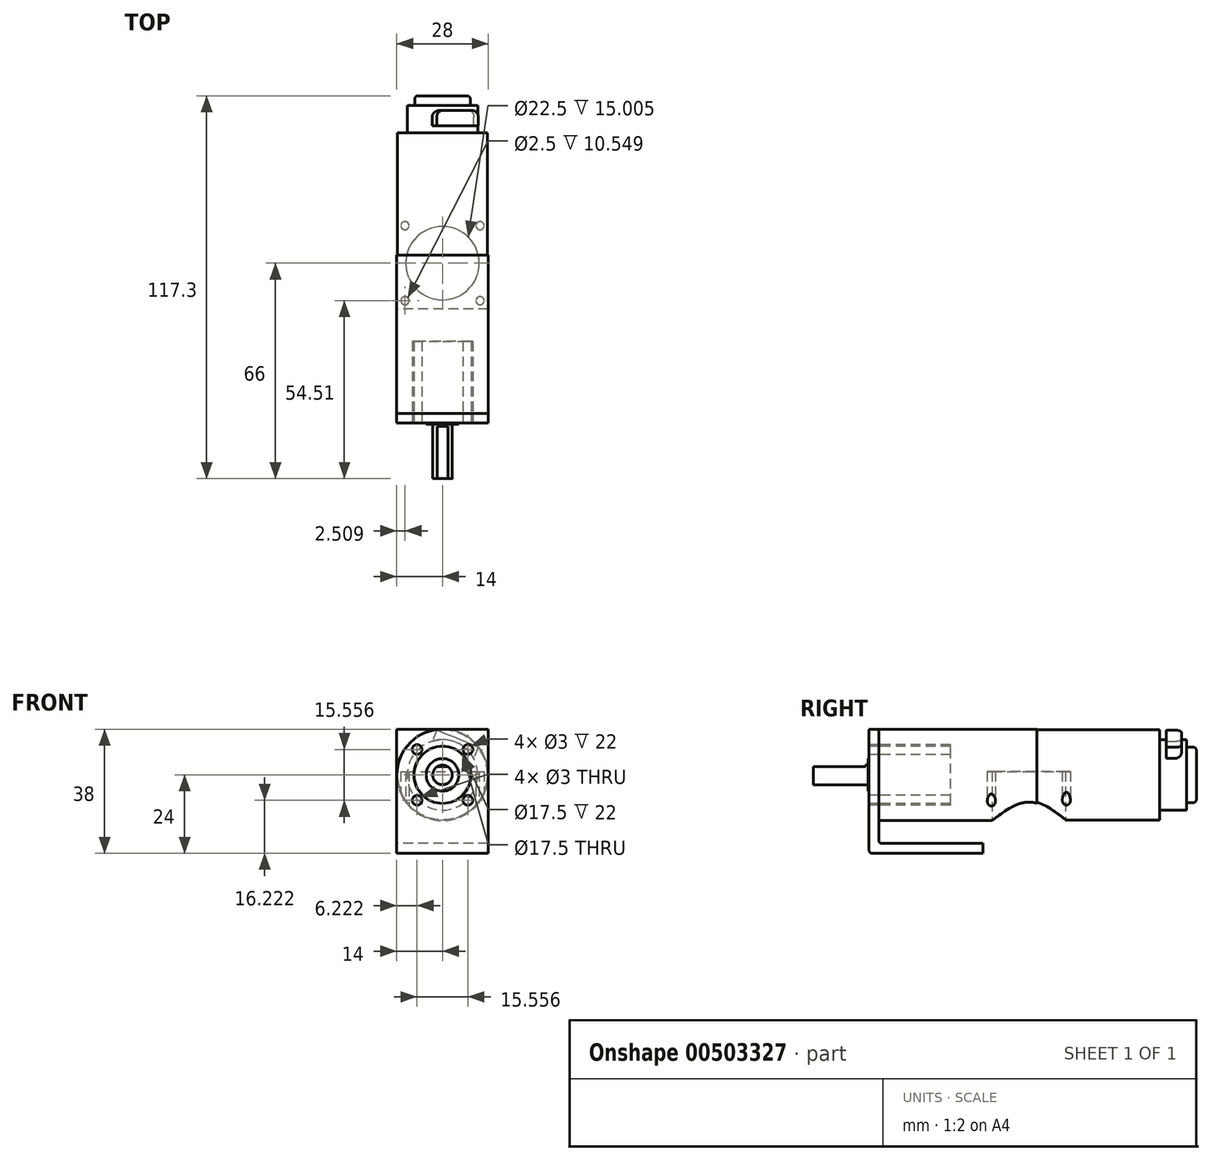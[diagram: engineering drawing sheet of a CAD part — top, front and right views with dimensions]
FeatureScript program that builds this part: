
annotation { "Feature Type Name" : "Feature", "Feature Type Description" : "" }
export const myFeature = defineFeature(function(context is Context, id is Id, definition is map)
    precondition{}
    {
        {
            var Q0;
            Q0=qCreatedBy(makeId("Right.planeOp"),FACE);
            var sketch = newSketch(context, id + "F0", { "sketchPlane" : qUnion([Q0])});
            skLineSegment(sketch, "E0", {"start": v(0, 0) * mm, "end": v(-20, 0) * mm});
            skLineSegment(sketch, "E1", {"start": v(-20, 0) * mm, "end": v(-20, 3) * mm});
            skLineSegment(sketch, "E2", {"start": v(-20, 3) * mm, "end": v(-3.3, 3) * mm});
            skLineSegment(sketch, "E3", {"start": v(-3.3, 3) * mm, "end": v(-3.3, 5) * mm});
            skLineSegment(sketch, "E4", {"start": v(-3.3, 5) * mm, "end": v(-2, 5) * mm});
            skLineSegment(sketch, "E5", {"start": v(-2, 5) * mm, "end": v(-2, 8.5) * mm});
            skLineSegment(sketch, "E6", {"start": v(-2, 8.5) * mm, "end": v(0, 8.5) * mm});
            skLineSegment(sketch, "E7", {"start": v(0, 8.5) * mm, "end": v(0, 14) * mm});
            skLineSegment(sketch, "E8", {"start": v(0, 14) * mm, "end": v(48.5, 14) * mm});
            skLineSegment(sketch, "E9", {"start": v(48.5, 14) * mm, "end": v(48.5, 13.8) * mm});
            skLineSegment(sketch, "E10", {"start": v(48.5, 13.8) * mm, "end": v(86, 13.8) * mm});
            skLineSegment(sketch, "E11", {"start": v(86, 13.8) * mm, "end": v(86, 10.8) * mm});
            skLineSegment(sketch, "E12", {"start": v(86, 10.8) * mm, "end": v(94.3, 10.8) * mm});
            skLineSegment(sketch, "E13", {"start": v(94.3, 10.8) * mm, "end": v(94.3, 8.5) * mm});
            skLineSegment(sketch, "E14", {"start": v(94.3, 8.5) * mm, "end": v(97.3, 8.5) * mm});
            skLineSegment(sketch, "E15", {"start": v(97.3, 8.5) * mm, "end": v(97.3, 0) * mm});
            skLineSegment(sketch, "E16", {"start": v(97.3, 0) * mm, "end": v(0, 0) * mm});
            skSolve(sketch);
        }
        {
            var Q0;
            Q0=makeQuery(id+"F0.imprint","IMPRINT",FACE,{"disambiguationData":[TD([[makeQuery(id+"F0.imprint","IMPRINT",EDGE,{"derivedFrom":sQuery(id+"F0.wireOp",EDGE,"E0")}),-1.0]])]});
            var Q1;
            Q1=sQuery(id+"F0.wireOp",EDGE,"E16");
            revolve(context, id + "F1", {"entities" : qUnion([Q0]), "axis" : qUnion([Q1]), "revolveType" : RevolveType.FULL});
        }
        {
            var Q0;
            Q0=makeQuery(id+"F1.opRevolve","SWEPT_FACE",FACE,{"disambiguationData":[OSD([sQuery(id+"F0.wireOp",EDGE,"E1")])]});
            var sketch = newSketch(context, id + "F2", { "sketchPlane" : qUnion([Q0])});
            skArc(sketch, "E17.0", {"start": v(1.66, 2.5) * mm, "mid": v(0, 3) * mm, "end": v(-1.66, 2.5) * mm});
            skLineSegment(sketch, "E18", {"start": v(-1.66, 2.5) * mm, "end": v(1.66, 2.5) * mm});
            skSolve(sketch);
        }
        {
            var Q0;
            Q0=makeQuery(id+"F2.imprint","IMPRINT",FACE,{"disambiguationData":[TD([[makeQuery(id+"F2.imprint","IMPRINT",EDGE,{"derivedFrom":sQuery(id+"F2.wireOp",EDGE,"E17.0")}),-1.0]])]});
            extrude(context, id + "F3", {"entities" : qUnion([Q0]), "operationType" : NewBodyOperationType.REMOVE, "oppositeDirection" : true, "depth" : 16 * mm});
        }
        {
            var Q0;
            Q0=makeQuery(id+"F1.opRevolve","SWEPT_FACE",FACE,{"disambiguationData":[OSD([sQuery(id+"F0.wireOp",EDGE,"E7")])]});
            var sketch = newSketch(context, id + "F4", { "sketchPlane" : qUnion([Q0])});
            skCircle(sketch, "E19", {"center": v(7.78, 7.78) * mm, "radius": 1.5 * mm});
            skCircle(sketch, "E20.1.0", {"center": v(-7.78, 7.78) * mm, "radius": 1.5 * mm});
            skCircle(sketch, "E20.2.0", {"center": v(-7.78, -7.78) * mm, "radius": 1.5 * mm});
            skCircle(sketch, "E20.3.0", {"center": v(7.78, -7.78) * mm, "radius": 1.5 * mm});
            skPoint(sketch, "E20.center", {"position": v(0, 0) * mm});
            skSolve(sketch);
        }
        {
            var Q0;
            Q0=makeQuery(id+"F4.imprint","IMPRINT",FACE,{"disambiguationData":[TD([[makeQuery(id+"F4.imprint","IMPRINT",EDGE,{"derivedFrom":sQuery(id+"F4.wireOp",EDGE,"E19")}),1.0]])]});
            extrude(context, id + "F5", {"entities" : qUnion([Q0]), "operationType" : NewBodyOperationType.REMOVE, "oppositeDirection" : true, "depth" : 3.5 * mm});
        }
        {
            var Q0;
            Q0=makeQuery(id+"F1.opRevolve","SWEPT_EDGE",EDGE,{"disambiguationData":[OSD([sQuery(id+"F0.wireOp",EDGE,"E14"),sQuery(id+"F0.wireOp",EDGE,"E15")])]});
            fillet(context, id + "F6", {"entities" : qUnion([Q0]), "radius" : 1 * mm, "tangentPropagation" : true, "allowEdgeOverflow" : false});
        }
        {
            var Q0;
            Q0=sQuery(id+"F0.wireOp",EDGE,"E16");
            cPlane(context, id + "F7", {"entities" : qUnion([Q0]), "cplaneType" : CPlaneType.LINE_ANGLE, "offset" : 25 * mm, "angle" : 157.5 * degree, "width" : 150 * mm, "height" : 150 * mm});
        }
        {
            var Q0;
            Q0=qCreatedBy(id+"F7.planeOp",FACE);
            var sketch = newSketch(context, id + "F8", { "sketchPlane" : qUnion([Q0])});
            skLineSegment(sketch, "E21.bottom", {"start": v(6.9, 92.79) * mm, "end": v(-6.9, 92.79) * mm});
            skLineSegment(sketch, "E21.top", {"start": v(6.9, 88.09) * mm, "end": v(-6.9, 88.09) * mm});
            skLineSegment(sketch, "E21.left", {"start": v(6.9, 92.79) * mm, "end": v(6.9, 88.09) * mm});
            skLineSegment(sketch, "E21.right", {"start": v(-6.9, 92.79) * mm, "end": v(-6.9, 88.09) * mm});
            skPoint(sketch, "E21.middle", {"position": v(0, 90.44) * mm});
            skSolve(sketch);
        }
        {
            var Q0;
            Q0=qSketchRegion(id+"F8",true);
            extrude(context, id + "F9", {"entities" : qUnion([Q0]), "operationType" : NewBodyOperationType.ADD, "depth" : 12 * mm});
        }
        {
            var Q0;
            Q0=makeQuery(id+"F9.opExtrude","SWEPT_EDGE",EDGE,{"disambiguationData":[OSD([sQuery(id+"F8.wireOp",EDGE,"E21.bottom"),sQuery(id+"F8.wireOp",EDGE,"E21.left")])]});
            var Q1;
            Q1=makeQuery(id+"F9.opExtrude","SWEPT_EDGE",EDGE,{"disambiguationData":[OSD([sQuery(id+"F8.wireOp",EDGE,"E21.bottom"),sQuery(id+"F8.wireOp",EDGE,"E21.right")])]});
            fillet(context, id + "F10", {"entities" : qUnion([Q0, Q1]), "radius" : 2 * mm, "tangentPropagation" : true, "allowEdgeOverflow" : false});
        }
        {
            var Q0;
            Q0=qCreatedBy(makeId("Right.planeOp"),FACE);
            var sketch = newSketch(context, id + "F11", { "sketchPlane" : qUnion([Q0])});
            skLineSegment(sketch, "E22.0", {"start": v(0, -21) * mm, "end": v(0, 14) * mm});
            skLineSegment(sketch, "E23.0", {"start": v(0, 0) * mm, "end": v(-20, 0) * mm, "construction": true});
            skLineSegment(sketch, "E24", {"start": v(0, 14) * mm, "end": v(-19.97, 14) * mm, "construction": true});
            skPoint(sketch, "E25.orphan", {"position": v(0, 14) * mm});
            skPoint(sketch, "E26.orphan", {"position": v(0, 8.5) * mm});
            skLineSegment(sketch, "E27", {"start": v(0, 14) * mm, "end": v(-3, 14) * mm});
            skLineSegment(sketch, "E28", {"start": v(-3, 14) * mm, "end": v(-3, -24) * mm});
            skLineSegment(sketch, "E29", {"start": v(-3, -24) * mm, "end": v(32, -24) * mm});
            skLineSegment(sketch, "E30", {"start": v(32, -24) * mm, "end": v(32, -21) * mm});
            skLineSegment(sketch, "E31", {"start": v(32, -21) * mm, "end": v(0, -21) * mm});
            skSolve(sketch);
        }
        {
            var Q0;
            Q0=makeQuery(id+"F11.imprint","IMPRINT",FACE,{"disambiguationData":[TD([[makeQuery(id+"F11.imprint","IMPRINT",EDGE,{"derivedFrom":sQuery(id+"F11.wireOp",EDGE,"E22.0")}),1.0]])]});
            extrude(context, id + "F12", {"entities" : qUnion([Q0]), "endBound" : BoundingType.SYMMETRIC, "depth" : 28 * mm, "hasSecondDirection" : true, "secondDirectionOppositeDirection" : true, "secondDirectionDepth" : 25 * mm});
        }
        {
            var Q0;
            Q0=makeQuery(id+"F12.opExtrude","SWEPT_EDGE",EDGE,{"disambiguationData":[OSD([sQuery(id+"F11.wireOp",EDGE,"E22.0"),sQuery(id+"F11.wireOp",EDGE,"E31")])]});
            var Q1;
            Q1=makeQuery(id+"F12.opExtrude","SWEPT_EDGE",EDGE,{"disambiguationData":[OSD([sQuery(id+"F11.wireOp",EDGE,"E28"),sQuery(id+"F11.wireOp",EDGE,"E29")])]});
            fillet(context, id + "F13", {"entities" : qUnion([Q0, Q1]), "radius" : 1 * mm, "tangentPropagation" : true, "allowEdgeOverflow" : false});
        }
        {
            var Q0;
            Q0=makeQuery(id+"F12.opExtrude","SWEPT_FACE",FACE,{"disambiguationData":[OSD([sQuery(id+"F11.wireOp",EDGE,"E28")])]});
            var sketch = newSketch(context, id + "F14", { "sketchPlane" : qUnion([Q0])});
            skPoint(sketch, "E32.0", {"position": v(0, 0) * mm});
            skCircle(sketch, "E33", {"center": v(0, 0) * mm, "radius": 8.75 * mm});
            skCircle(sketch, "E34", {"center": v(-7.78, 7.78) * mm, "radius": 1.5 * mm});
            skCircle(sketch, "E35.1.0", {"center": v(-7.78, -7.78) * mm, "radius": 1.5 * mm});
            skCircle(sketch, "E35.2.0", {"center": v(7.78, -7.78) * mm, "radius": 1.5 * mm});
            skCircle(sketch, "E35.3.0", {"center": v(7.78, 7.78) * mm, "radius": 1.5 * mm});
            skSolve(sketch);
        }
        {
            var Q0;
            Q0=qSketchRegion(id+"F14",true);
            extrude(context, id + "F15", {"entities" : qUnion([Q0]), "operationType" : NewBodyOperationType.REMOVE, "oppositeDirection" : true, "depth" : 25 * mm});
        }
        {
            var Q0;
            Q0=makeQuery(id+"F12.opExtrude","SWEPT_FACE",FACE,{"disambiguationData":[OSD([sQuery(id+"F11.wireOp",EDGE,"E29")])]});
            var sketch = newSketch(context, id + "F16", { "sketchPlane" : qUnion([Q0])});
            skLineSegment(sketch, "E36", {"start": v(0, -32) * mm, "end": v(0, -46) * mm, "construction": true});
            skCircle(sketch, "E37", {"center": v(0, -46) * mm, "radius": 11.25 * mm});
            skLineSegment(sketch, "E38", {"start": v(0, -46) * mm, "end": v(-11.5, -34.5) * mm, "construction": true});
            skCircle(sketch, "E39", {"center": v(-11.5, -34.5) * mm, "radius": 1.25 * mm});
            skCircle(sketch, "E40.1.0", {"center": v(-11.5, -57.5) * mm, "radius": 1.25 * mm});
            skCircle(sketch, "E40.2.0", {"center": v(11.5, -57.5) * mm, "radius": 1.25 * mm});
            skCircle(sketch, "E40.3.0", {"center": v(11.5, -34.5) * mm, "radius": 1.25 * mm});
            skSolve(sketch);
        }
        {
            var Q0;
            Q0=qSketchRegion(id+"F16",true);
            extrude(context, id + "F17", {"entities" : qUnion([Q0]), "operationType" : NewBodyOperationType.REMOVE, "oppositeDirection" : true, "depth" : 25 * mm});
        }
    });
